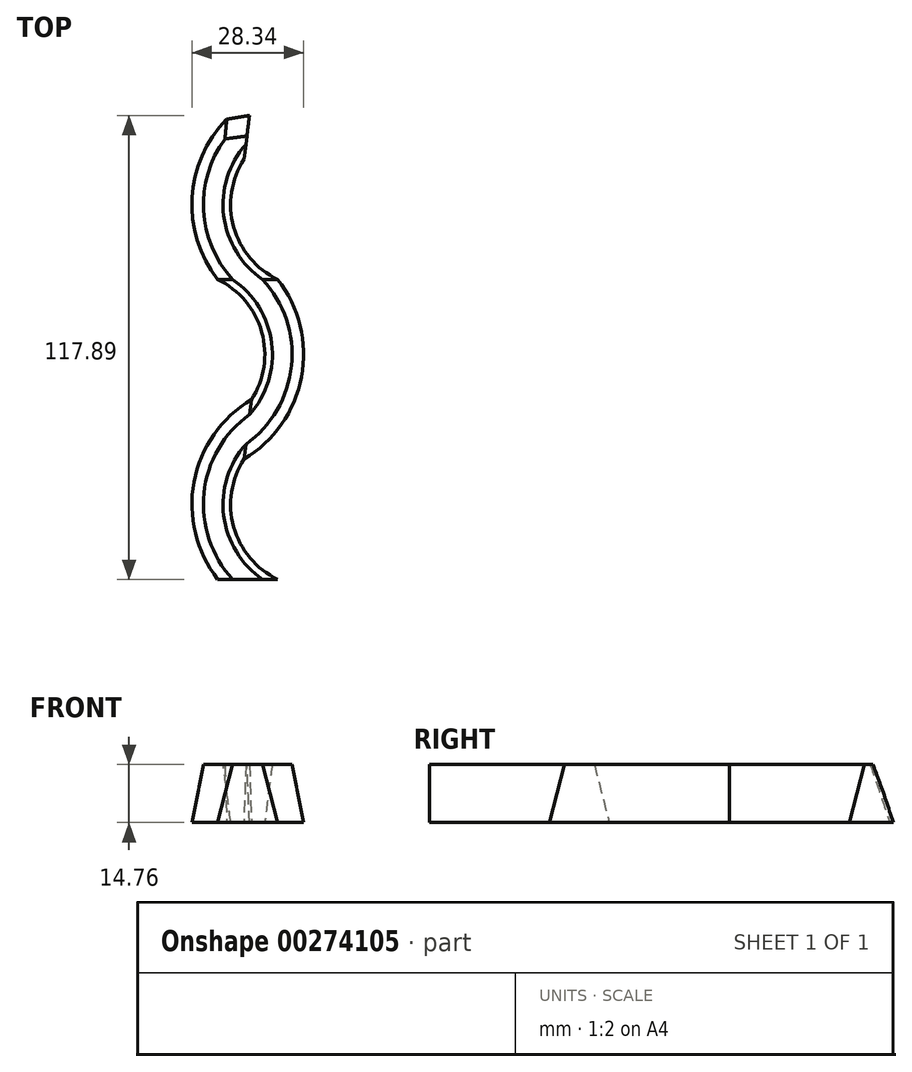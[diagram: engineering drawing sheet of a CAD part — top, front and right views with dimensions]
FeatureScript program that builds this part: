
annotation { "Feature Type Name" : "Feature", "Feature Type Description" : "" }
export const myFeature = defineFeature(function(context is Context, id is Id, definition is map)
    precondition{}
    {
        {
            var Q0;
            Q0=qCreatedBy(makeId("Top.planeOp"),FACE);
            var sketch = newSketch(context, id + "F0", { "sketchPlane" : qUnion([Q0])});
            skLineSegment(sketch, "E0", {"start": v(0, 0) * mm, "end": v(0, 114.3) * mm});
            skLineSegment(sketch, "E1", {"start": v(0, 0) * mm, "end": v(0, 38.1) * mm});
            skLineSegment(sketch, "E2", {"start": v(0, 38.1) * mm, "end": v(0, 76.2) * mm});
            skLineSegment(sketch, "E3", {"start": v(0, 76.2) * mm, "end": v(0, 114.3) * mm});
            skArc(sketch, "E4", {"start": v(0, 38.1) * mm, "mid": v(-8.6, 19.05) * mm, "end": v(0, 0) * mm});
            skArc(sketch, "E5", {"start": v(0, 38.1) * mm, "mid": v(8.6, 57.15) * mm, "end": v(0, 76.2) * mm});
            skArc(sketch, "E6", {"start": v(0, 114.3) * mm, "mid": v(-8.6, 95.25) * mm, "end": v(0, 76.2) * mm});
            skLineSegment(sketch, "E7", {"start": v(0, 114.3) * mm, "end": v(0, 152.4) * mm});
            skArc(sketch, "E8", {"start": v(0, 114.3) * mm, "mid": v(8.6, 133.35) * mm, "end": v(0, 152.4) * mm});
            skSolve(sketch);
        }
        {
            var Q0;
            Q0=qCreatedBy(makeId("Front.planeOp"),FACE);
            var sketch = newSketch(context, id + "F1", { "sketchPlane" : qUnion([Q0])});
            skLineSegment(sketch, "E9", {"start": v(-3.81, 0) * mm, "end": v(3.81, 0) * mm});
            skLineSegment(sketch, "E10", {"start": v(-3.81, 0) * mm, "end": v(-7.62, -14.76) * mm});
            skLineSegment(sketch, "E11", {"start": v(-7.62, -14.76) * mm, "end": v(0, -14.76) * mm});
            skLineSegment(sketch, "E12.MirrorCS", {"start": v(7.62, -14.76) * mm, "end": v(0, -14.76) * mm});
            skLineSegment(sketch, "E13.MirrorCS", {"start": v(3.81, 0) * mm, "end": v(7.62, -14.76) * mm});
            skSolve(sketch);
        }
        {
            var Q0;
            Q0=makeQuery(id+"F1.imprint","IMPRINT",FACE,{"disambiguationData":[TD([[makeQuery(id+"F1.imprint","IMPRINT",EDGE,{"derivedFrom":sQuery(id+"F1.wireOp",EDGE,"E9")}),-1.0]])]});
            var Q1;
            Q1=sQuery(id+"F0.wireOp",EDGE,"E4");
            var Q2;
            Q2=sQuery(id+"F0.wireOp",EDGE,"E5");
            var Q3;
            Q3=sQuery(id+"F0.wireOp",EDGE,"E6");
            sweep(context, id + "F2", {"profiles" : qUnion([Q0]), "path" : qUnion([Q1, Q2, Q3])});
        }
        {
            var Q0;
            Q0=makeQuery(id+"F2.opSweep","CAP_EDGE",EDGE,{"disambiguationData":[OSD([sQuery(id+"F0.wireOp",VERTEX,"E6.start"),sQuery(id+"F1.wireOp",EDGE,"E10")])],"isStart":false});
            chamfer(context, id + "F3", {"entities" : qUnion([Q0]), "chamferType" : ChamferType.TWO_OFFSETS, "width1" : 2.54 * mm, "oppositeDirection" : false, "width2" : 7.62 * mm, "tangentPropagation" : true});
        }
    });
